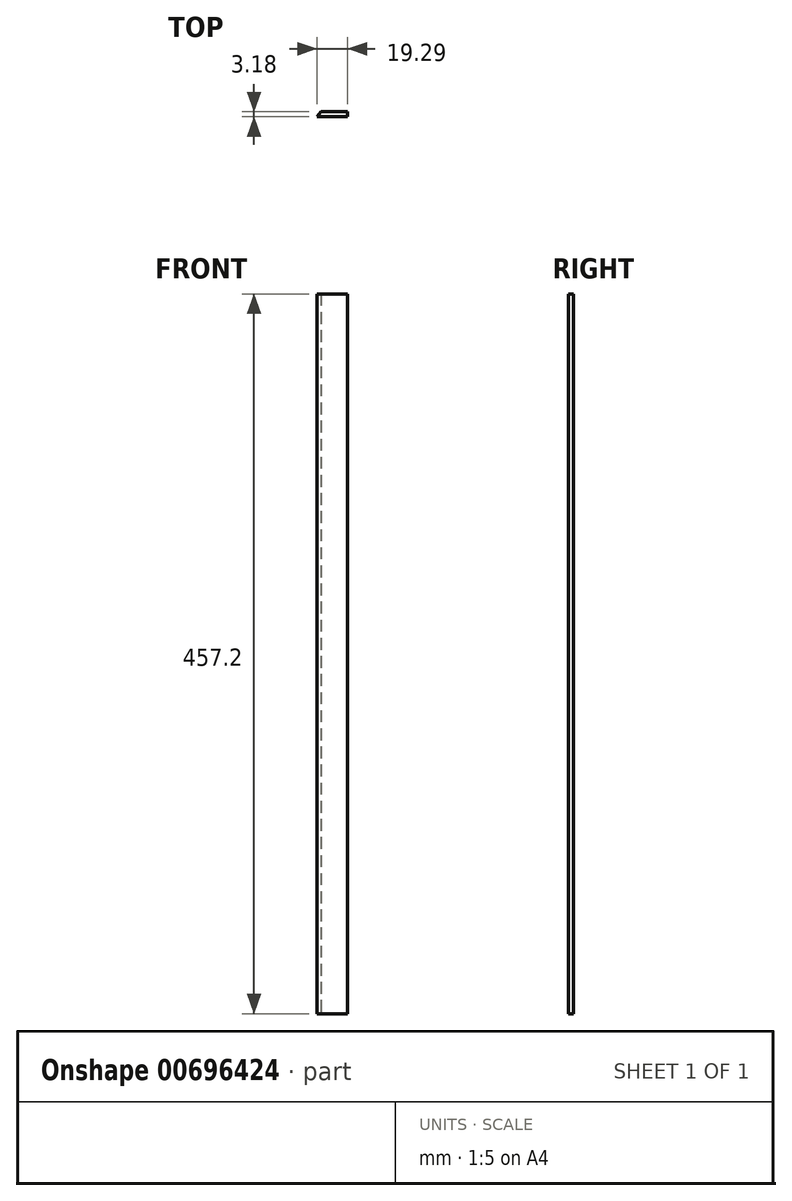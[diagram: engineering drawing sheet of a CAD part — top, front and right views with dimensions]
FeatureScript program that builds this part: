
annotation { "Feature Type Name" : "Feature", "Feature Type Description" : "" }
export const myFeature = defineFeature(function(context is Context, id is Id, definition is map)
    precondition{}
    {
        {
            var Q0;
            Q0=qCreatedBy(makeId("Top.planeOp"),FACE);
            var sketch = newSketch(context, id + "F0", { "sketchPlane" : qUnion([Q0])});
            skLineSegment(sketch, "E0", {"start": v(0, 0) * mm, "end": v(-9.55, 0) * mm});
            skLineSegment(sketch, "E1", {"start": v(-9.55, 0) * mm, "end": v(-31.5, 26.17) * mm});
            skLineSegment(sketch, "E2", {"start": v(-31.5, 26.17) * mm, "end": v(0, 26.17) * mm});
            skLineSegment(sketch, "E3", {"start": v(0, 26.17) * mm, "end": v(0, 23) * mm});
            skLineSegment(sketch, "E4", {"start": v(0, 23) * mm, "end": v(16.63, 23) * mm});
            skLineSegment(sketch, "E5", {"start": v(1.62, 0) * mm, "end": v(16.63, 0) * mm});
            skLineSegment(sketch, "E6", {"start": v(16.63, 0) * mm, "end": v(16.63, 3.18) * mm});
            skLineSegment(sketch, "E7", {"start": v(16.63, 3.18) * mm, "end": v(0, 3.18) * mm});
            skLineSegment(sketch, "E8", {"start": v(0, 3.18) * mm, "end": v(16.63, 23) * mm});
            skLineSegment(sketch, "E9", {"start": v(1.62, 0) * mm, "end": v(0, 0) * mm});
            skLineSegment(sketch, "E10", {"start": v(0, 3.18) * mm, "end": v(19.3, 26.17) * mm});
            skLineSegment(sketch, "E11", {"start": v(19.3, 26.17) * mm, "end": v(0, 26.17) * mm});
            skLineSegment(sketch, "E12", {"start": v(19.3, 26.17) * mm, "end": v(-2.66, 0) * mm});
            skPoint(sketch, "E12.endSnap0", {"position": v(-4.78, 0) * mm});
            skSolve(sketch);
        }
        {
            var Q0;
            Q0=makeQuery(id+"F0.imprint","IMPRINT",FACE,{"disambiguationData":[TD([[makeQuery(id+"F0.imprint","IMPRINT",EDGE,{"derivedFrom":sQuery(id+"F0.wireOp",EDGE,"E0")}),-1.0]])]});
            extrude(context, id + "F1", {"entities" : qUnion([Q0]), "depth" : 457.2 * mm, "offsetDistance" : 25.4 * mm});
        }
    });
